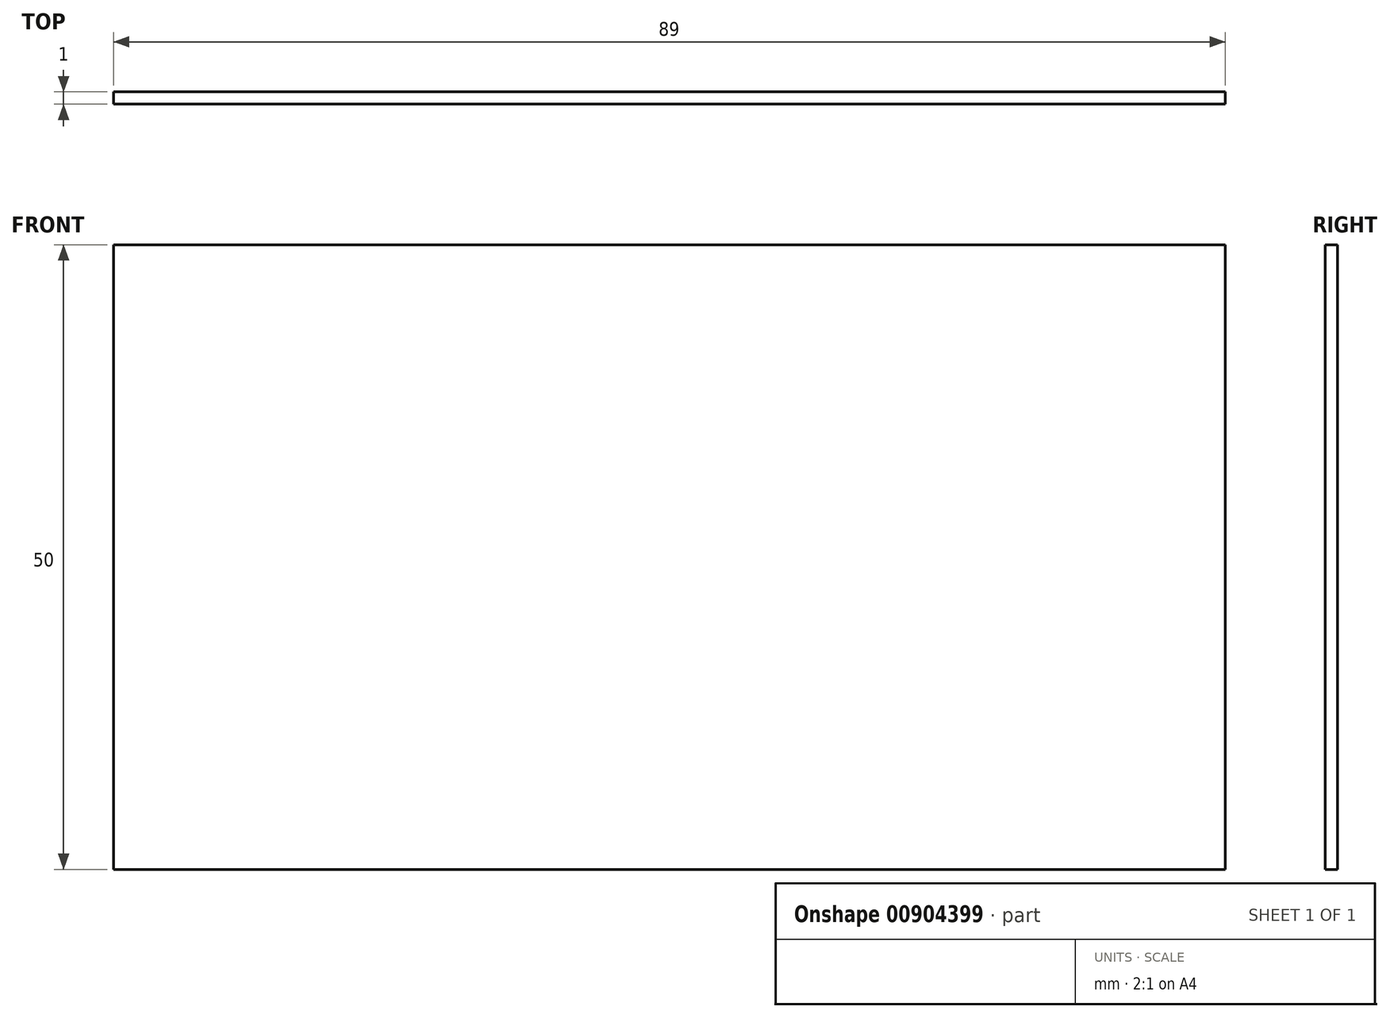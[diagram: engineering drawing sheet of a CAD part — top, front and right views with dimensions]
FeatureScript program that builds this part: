
annotation { "Feature Type Name" : "Feature", "Feature Type Description" : "" }
export const myFeature = defineFeature(function(context is Context, id is Id, definition is map)
    precondition{}
    {
        {
            var Q0;
            Q0=qCreatedBy(makeId("Front.planeOp"),FACE);
            var sketch = newSketch(context, id + "F0", { "sketchPlane" : qUnion([Q0])});
            skLineSegment(sketch, "E0.bottom", {"start": v(-44.5, 25) * mm, "end": v(44.5, 25) * mm});
            skLineSegment(sketch, "E0.top", {"start": v(-44.5, -25) * mm, "end": v(44.5, -25) * mm});
            skLineSegment(sketch, "E0.left", {"start": v(-44.5, 25) * mm, "end": v(-44.5, -25) * mm});
            skLineSegment(sketch, "E0.right", {"start": v(44.5, 25) * mm, "end": v(44.5, -25) * mm});
            skSolve(sketch);
        }
        {
            var Q0;
            Q0 = qSketchRegion(id + "F0", true);
            extrude(context, id + "F1", {"entities" : qUnion([Q0]), "oppositeDirection" : true, "depth" : 1 * mm, "offsetDistance" : 25 * mm});
        }
    });
